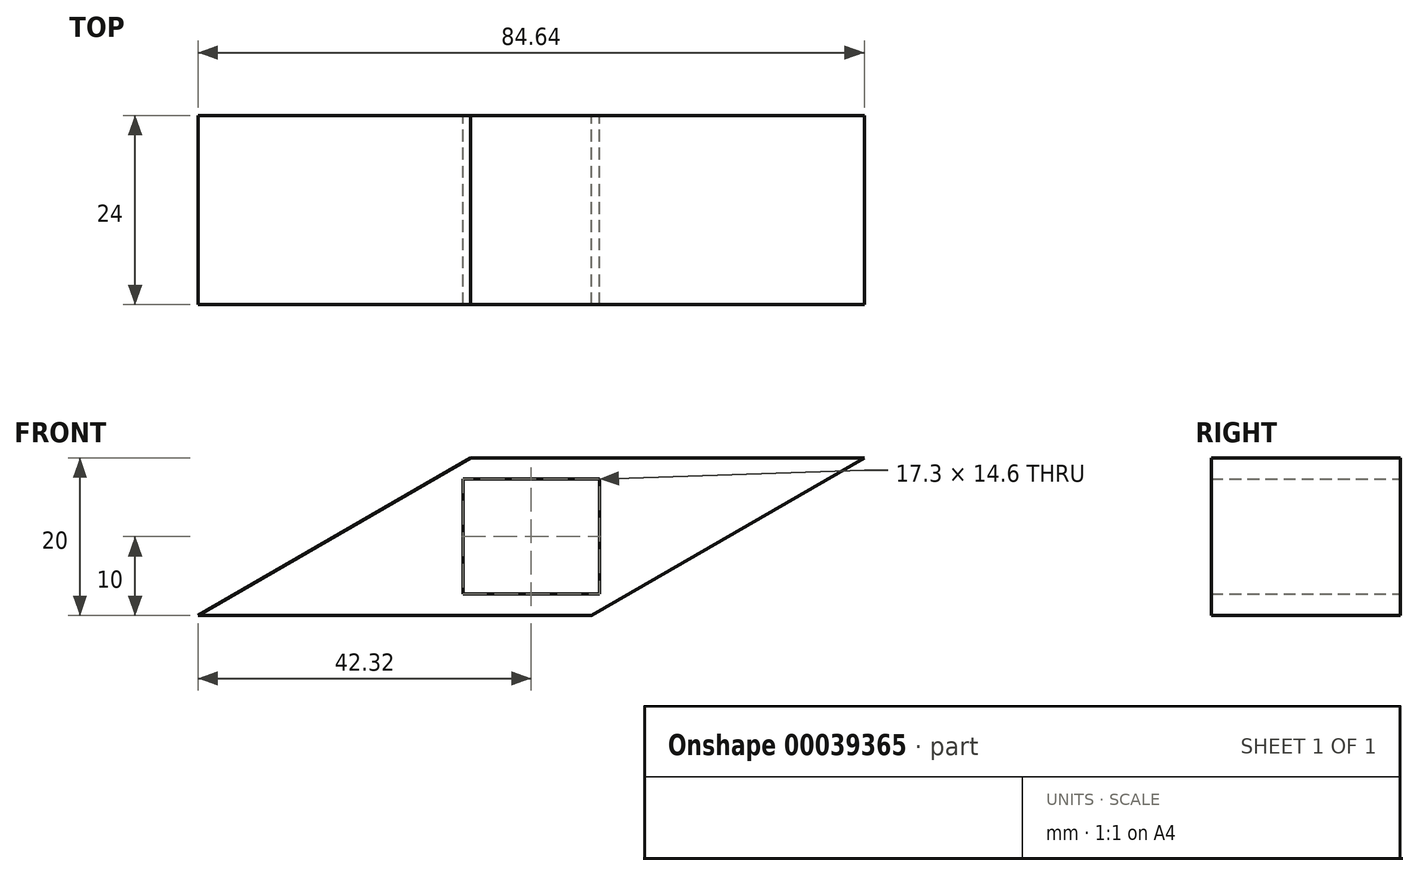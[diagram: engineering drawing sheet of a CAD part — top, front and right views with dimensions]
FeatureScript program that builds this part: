
annotation { "Feature Type Name" : "Feature", "Feature Type Description" : "" }
export const myFeature = defineFeature(function(context is Context, id is Id, definition is map)
    precondition{}
    {
        {
            var Q0;
            Q0=qCreatedBy(makeId("Front.planeOp"),FACE);
            var sketch = newSketch(context, id + "F0", { "sketchPlane" : qUnion([Q0])});
            skLineSegment(sketch, "E0.rect.bottom", {"start": v(-7.68, 10) * mm, "end": v(42.32, 10) * mm});
            skLineSegment(sketch, "E0.rect.top", {"start": v(-42.32, -10) * mm, "end": v(7.68, -10) * mm});
            skLineSegment(sketch, "E0.rect.left", {"start": v(-7.68, 10) * mm, "end": v(-42.32, -10) * mm});
            skLineSegment(sketch, "E0.rect.right", {"start": v(42.32, 10) * mm, "end": v(7.68, -10) * mm});
            skPoint(sketch, "E0.rect.middle", {"position": v(0, 0) * mm});
            skLineSegment(sketch, "E1.rect.bottom", {"start": v(-8.65, 7.3) * mm, "end": v(8.65, 7.3) * mm});
            skLineSegment(sketch, "E1.rect.top", {"start": v(-8.65, -7.3) * mm, "end": v(8.65, -7.3) * mm});
            skLineSegment(sketch, "E1.rect.left", {"start": v(-8.65, 7.3) * mm, "end": v(-8.65, -7.3) * mm});
            skLineSegment(sketch, "E1.rect.right", {"start": v(8.65, 7.3) * mm, "end": v(8.65, -7.3) * mm});
            skSolve(sketch);
        }
        {
            var Q0;
            Q0=makeQuery(id+"F0.imprint","IMPRINT",FACE,{"disambiguationData":[TD([[makeQuery(id+"F0.imprint","IMPRINT",EDGE,{"derivedFrom":sQuery(id+"F0.wireOp",EDGE,"E0.rect.bottom")}),-1.0]])]});
            extrude(context, id + "F1", {"entities" : qUnion([Q0]), "depth" : 24 * mm});
        }
    });
